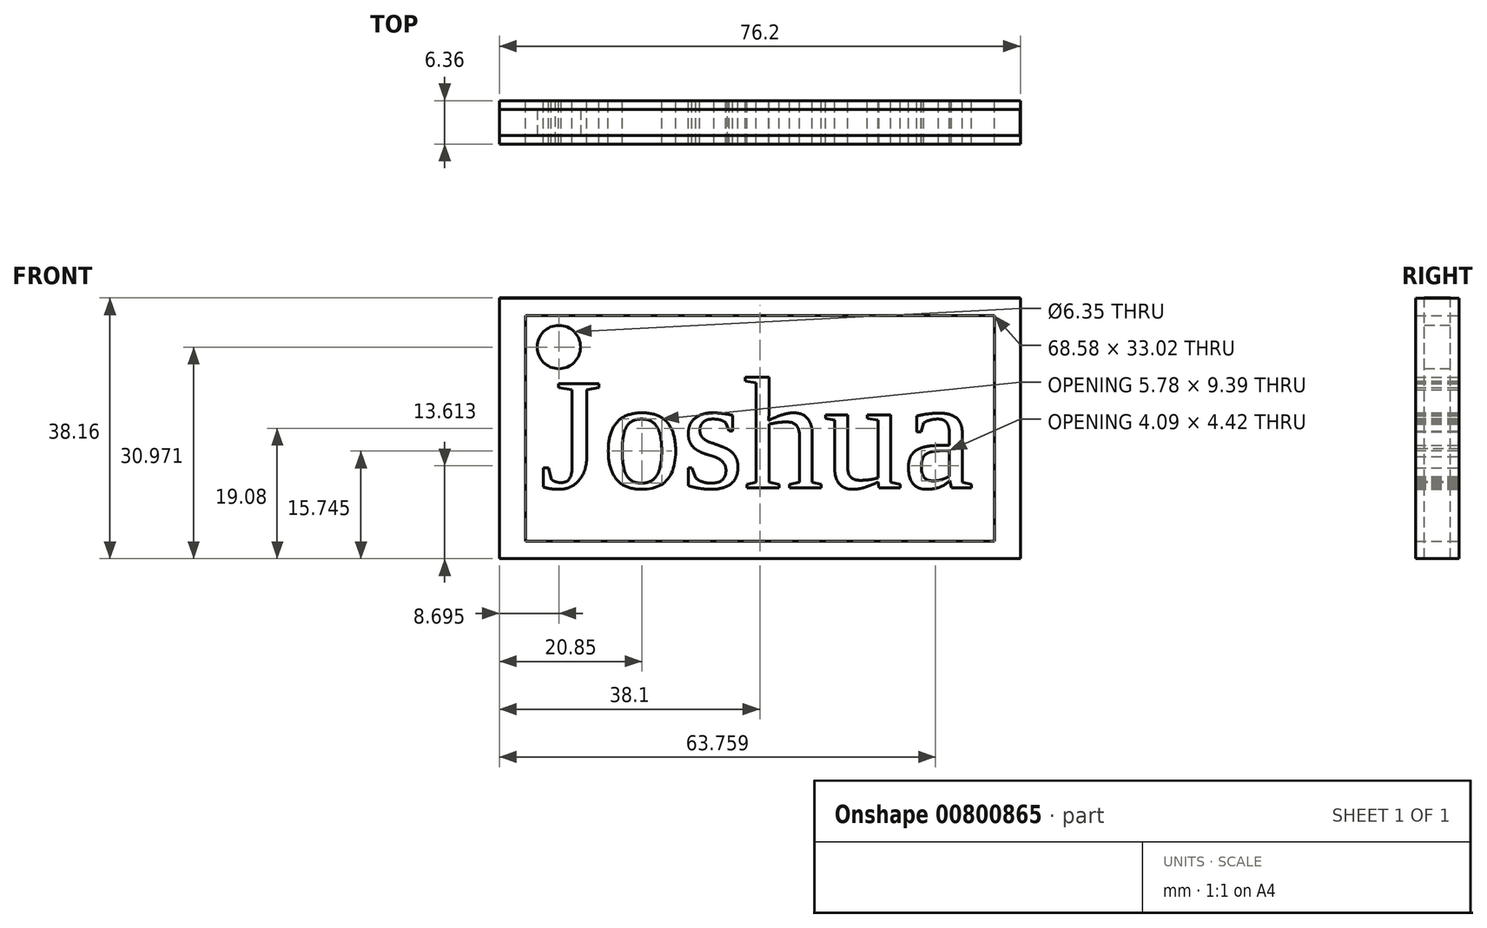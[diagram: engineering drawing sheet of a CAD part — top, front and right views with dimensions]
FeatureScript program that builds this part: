
annotation { "Feature Type Name" : "Feature", "Feature Type Description" : "" }
export const myFeature = defineFeature(function(context is Context, id is Id, definition is map)
    precondition{}
    {
        {
            var Q0;
            Q0=qCreatedBy(makeId("Front.planeOp"),FACE);
            var sketch = newSketch(context, id + "F0", { "sketchPlane" : qUnion([Q0])});
            skLineSegment(sketch, "E0.bottom", {"start": v(38.1, -19.05) * mm, "end": v(-38.1, -19.05) * mm});
            skLineSegment(sketch, "E0.top", {"start": v(38.1, 19.05) * mm, "end": v(-38.1, 19.05) * mm});
            skLineSegment(sketch, "E0.left", {"start": v(38.1, -19.05) * mm, "end": v(38.1, 19.05) * mm});
            skLineSegment(sketch, "E0.right", {"start": v(-38.1, -19.05) * mm, "end": v(-38.1, 19.05) * mm});
            skPoint(sketch, "E0.middle", {"position": v(0, 0) * mm});
            skLineSegment(sketch, "E1.bottom", {"start": v(34.3, -16.51) * mm, "end": v(-34.3, -16.51) * mm});
            skLineSegment(sketch, "E1.top", {"start": v(34.3, 16.51) * mm, "end": v(-34.3, 16.51) * mm});
            skLineSegment(sketch, "E1.left", {"start": v(34.3, -16.51) * mm, "end": v(34.3, 16.51) * mm});
            skLineSegment(sketch, "E1.right", {"start": v(-34.3, -16.51) * mm, "end": v(-34.3, 16.51) * mm});
            skSolve(sketch);
        }
        {
            var Q0;
            Q0=qCreatedBy(makeId("Front.planeOp"),FACE);
            var sketch = newSketch(context, id + "F1", { "sketchPlane" : qUnion([Q0])});
            skText(sketch, "E2", { "text": "Joshua", "fontName": "Tinos-Regular.ttf"});
            const initialGuessF1  = {"E2": [-0.03213, -0.0087, 1, 0, 0.01676]};
            skSetInitialGuess(sketch, initialGuessF1);
            skSolve(sketch);
        }
        {
            var Q0;
            Q0=makeQuery(id+"F0.imprint","IMPRINT",FACE,{"disambiguationData":[TD([[makeQuery(id+"F0.imprint","IMPRINT",EDGE,{"derivedFrom":sQuery(id+"F0.wireOp",EDGE,"E0.bottom")}),-1.0]])]});
            extrude(context, id + "F2", {"entities" : qUnion([Q0]), "depth" : 6.35 * mm, "offsetDistance" : 25.4 * mm, "symmetric" : true});
        }
        {
            var Q0;
            Q0=qSketchRegion(id+"F1",true);
            extrude(context, id + "F3", {"entities" : qUnion([Q0]), "depth" : 6.35 * mm, "offsetDistance" : 25.4 * mm, "symmetric" : true});
        }
        {
            var Q0;
            Q0=makeQuery(id+"F0.imprint","IMPRINT",FACE,{"disambiguationData":[TD([[makeQuery(id+"F0.imprint","IMPRINT",EDGE,{"derivedFrom":sQuery(id+"F0.wireOp",EDGE,"E1.bottom")}),-1.0]])]});
            var sketch = newSketch(context, id + "F4", { "sketchPlane" : qUnion([Q0])});
            skLineSegment(sketch, "E3.bottom", {"start": v(-38.07, -19.08) * mm, "end": v(38.07, -19.08) * mm});
            skLineSegment(sketch, "E3.top", {"start": v(-38.07, 19.08) * mm, "end": v(38.07, 19.08) * mm});
            skLineSegment(sketch, "E3.left", {"start": v(-38.07, -19.08) * mm, "end": v(-38.07, 19.08) * mm});
            skLineSegment(sketch, "E3.right", {"start": v(38.07, -19.08) * mm, "end": v(38.07, 19.08) * mm});
            skPoint(sketch, "E3.middle", {"position": v(0, 0) * mm});
            skSolve(sketch);
        }
        {
            var Q0;
            Q0 = qSketchRegion(id + "F4", true);
            extrude(context, id + "F5", {"entities" : qUnion([Q0]), "depth" : 3.8 * mm, "offsetDistance" : 25.4 * mm, "symmetric" : true});
        }
        {
            var Q0;
            Q0=makeQuery(id+"F2.opExtrude","CAP_FACE",FACE,{"disambiguationData":[OSD([sQuery(id+"F0.wireOp",EDGE,"E0.bottom"),sQuery(id+"F0.wireOp",EDGE,"E0.top"),sQuery(id+"F0.wireOp",EDGE,"E0.left"),sQuery(id+"F0.wireOp",EDGE,"E0.right"),sQuery(id+"F0.wireOp",EDGE,"E1.bottom"),sQuery(id+"F0.wireOp",EDGE,"E1.top"),sQuery(id+"F0.wireOp",EDGE,"E1.left"),sQuery(id+"F0.wireOp",EDGE,"E1.right")])],"isStart":false});
            var sketch = newSketch(context, id + "F6", { "sketchPlane" : qUnion([Q0])});
            skCircle(sketch, "E4", {"center": v(-29.4, 11.9) * mm, "radius": 2.97 * mm});
            skSolve(sketch);
        }
        {
            var Q0;
            Q0=sQuery(id+"F6.wireOp",VERTEX,"E4.center");
            var Q1;
            Q1=makeQuery(id+"F5.opExtrude","SWEPT_BODY",BODY,{"disambiguationData":[OSD([sQuery(id+"F4.wireOp",EDGE,"E3.bottom"),sQuery(id+"F4.wireOp",EDGE,"E3.top"),sQuery(id+"F4.wireOp",EDGE,"E3.left"),sQuery(id+"F4.wireOp",EDGE,"E3.right")])]});
            hole(context, id + "F7", {"style" : HoleStyle.SIMPLE, "endStyle" : HoleEndStyle.THROUGH, "holeDiameter" : 6.35 * mm, "majorDiameter" : 6.35 * mm, "isTappedThrough" : true, "tappedDepth" : 12.7 * mm, "tapClearance" : 3, "locations" : qUnion([Q0]), "scope" : qUnion([Q1])});
        }
    });
